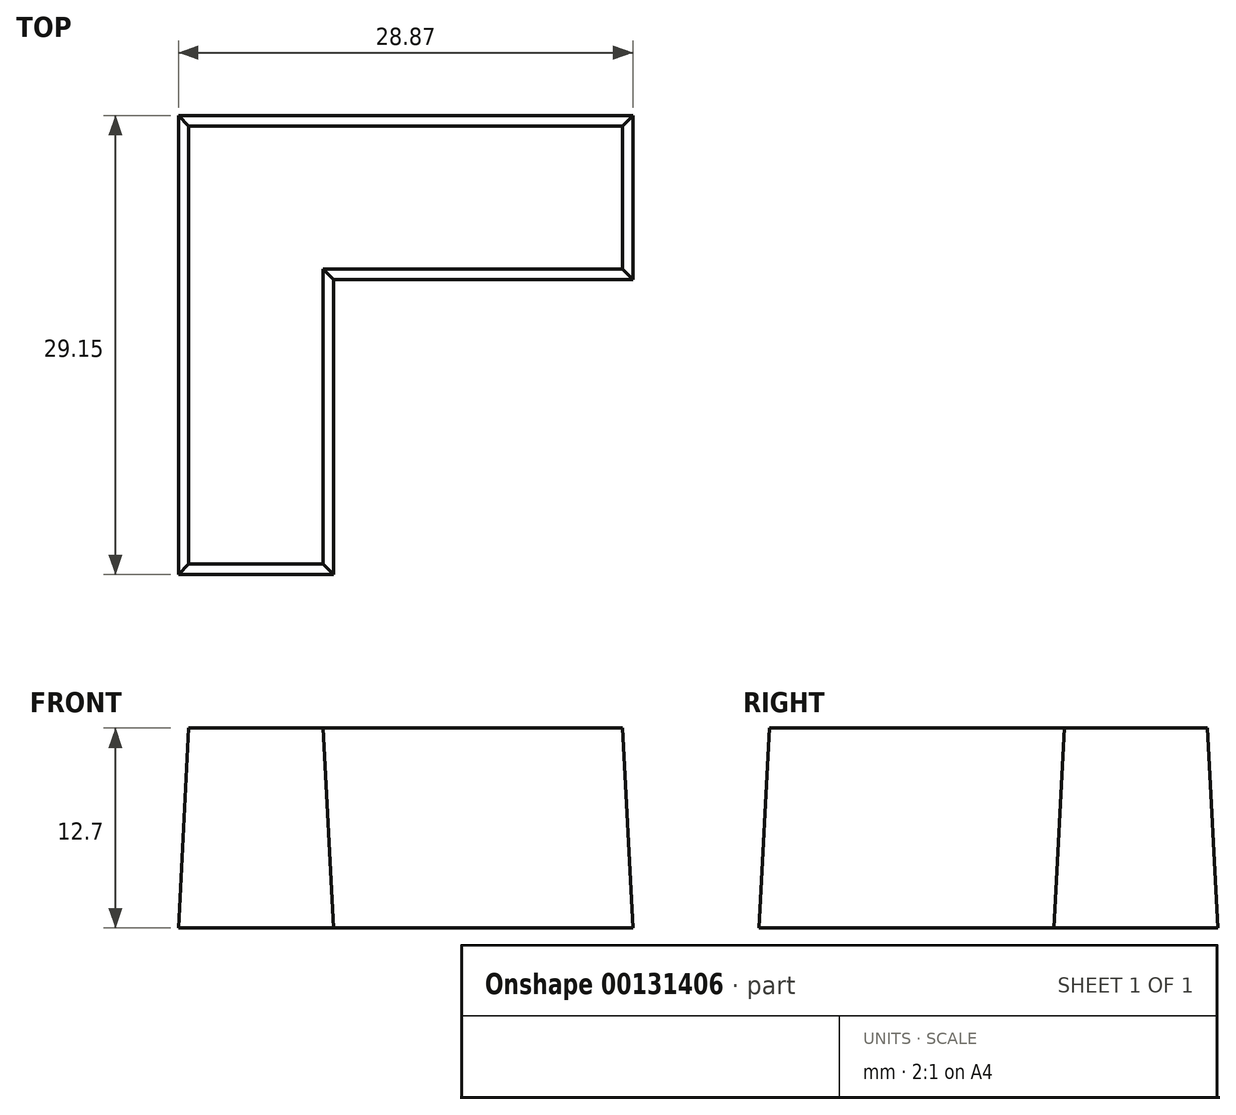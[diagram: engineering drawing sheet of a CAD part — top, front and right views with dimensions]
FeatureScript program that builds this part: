
annotation { "Feature Type Name" : "Feature", "Feature Type Description" : "" }
export const myFeature = defineFeature(function(context is Context, id is Id, definition is map)
    precondition{}
    {
        {
            var Q0;
            Q0=qCreatedBy(makeId("Top.planeOp"),FACE);
            var sketch = newSketch(context, id + "F0", { "sketchPlane" : qUnion([Q0])});
            skLineSegment(sketch, "E0", {"start": v(-13.6, 25.19) * mm, "end": v(15.27, 25.19) * mm});
            skLineSegment(sketch, "E1", {"start": v(15.27, 25.19) * mm, "end": v(15.27, 14.78) * mm});
            skLineSegment(sketch, "E2", {"start": v(15.27, 14.78) * mm, "end": v(-3.75, 14.78) * mm});
            skLineSegment(sketch, "E3", {"start": v(-3.75, 14.78) * mm, "end": v(-3.75, -3.96) * mm});
            skLineSegment(sketch, "E4", {"start": v(-3.75, -3.96) * mm, "end": v(-13.6, -3.96) * mm});
            skLineSegment(sketch, "E5", {"start": v(-13.6, -3.96) * mm, "end": v(-13.6, 25.19) * mm});
            skSolve(sketch);
        }
        {
            var Q0;
            Q0 = qSketchRegion(id + "F0", true);
            extrude(context, id + "F1", {"entities" : qUnion([Q0]), "flatOperationType" : FlatOperationType.REMOVE, "offsetDistance" : 25.4 * mm, "depth" : 12.7 * mm, "hasDraft" : true, "draftAngle" : 3 * degree, "draftPullDirection" : true, "domain" : OperationDomain.MODEL});
        }
    });
